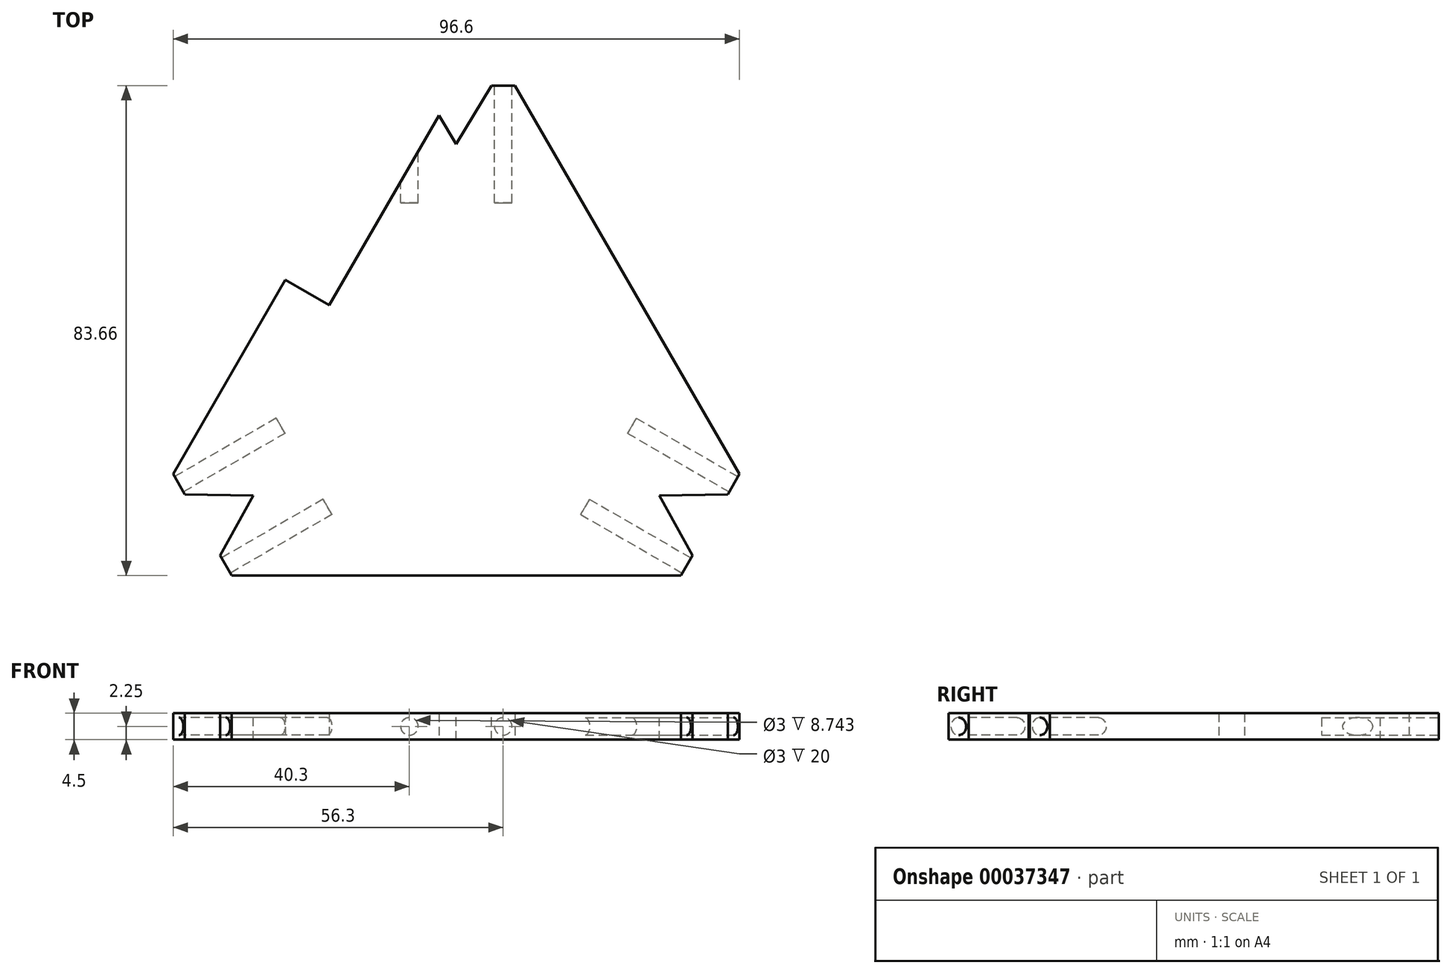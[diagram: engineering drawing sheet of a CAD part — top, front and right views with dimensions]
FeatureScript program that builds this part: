
annotation { "Feature Type Name" : "Feature", "Feature Type Description" : "" }
export const myFeature = defineFeature(function(context is Context, id is Id, definition is map)
    precondition{}
    {
        {
            var Q0;
            Q0=qCreatedBy(makeId("Top.planeOp"),FACE);
            var sketch = newSketch(context, id + "F0", { "sketchPlane" : qUnion([Q0])});
            skLineSegment(sketch, "E0.0", {"start": v(0, 50) * mm, "end": v(43.3, -25) * mm});
            skLineSegment(sketch, "E0.1", {"start": v(43.3, -25) * mm, "end": v(-43.3, -25) * mm});
            skCircle(sketch, "E1.cCircle", {"center": v(0, 0) * mm, "radius": 50 * mm, "construction": true});
            skLineSegment(sketch, "E1.0", {"start": v(-10, 50) * mm, "end": v(10, 50) * mm});
            skLineSegment(sketch, "E1.2", {"start": v(48.3, -16.34) * mm, "end": v(38.3, -33.66) * mm});
            skLineSegment(sketch, "E1.4", {"start": v(-38.3, -33.66) * mm, "end": v(-48.3, -16.34) * mm});
            skLineSegment(sketch, "E2", {"start": v(-10, 50) * mm, "end": v(-48.3, -16.34) * mm});
            skLineSegment(sketch, "E3", {"start": v(0, 50) * mm, "end": v(0, 0) * mm});
            skLineSegment(sketch, "E4.0.MirrorCS", {"start": v(10, 50) * mm, "end": v(48.3, -16.34) * mm});
            skLineSegment(sketch, "E5", {"start": v(-38.3, -33.66) * mm, "end": v(38.3, -33.66) * mm});
            skLineSegment(sketch, "E6", {"start": v(29.15, 16.83) * mm, "end": v(-43.3, -25) * mm});
            skLineSegment(sketch, "E7", {"start": v(43.3, -25) * mm, "end": v(-29.15, 16.83) * mm});
            skLineSegment(sketch, "E8.4.MirrorCS", {"start": v(0, 50) * mm, "end": v(-43.3, -25) * mm});
            skLineSegment(sketch, "E8.7.MirrorCS", {"start": v(-48.3, -16.34) * mm, "end": v(-38.3, -33.66) * mm});
            skLineSegment(sketch, "E9.11.MirrorCS", {"start": v(38.3, -33.66) * mm, "end": v(48.3, -16.34) * mm});
            skSolve(sketch);
        }
        {
            var Q0;
            {var subQ1=sQuery(id+"F0.wireOp",EDGE,"E0.1");var subQ4=sQuery(id+"F0.wireOp",EDGE,"c58d0613-940e-401f-9838-6fef4ca887ab.4.MirrorC");var subQ6=makeQuery(id+"F0.imprint","INTERSECT",VERTEX,{"disambiguationData":[OD(0.0)],"derivedFrom":[subQ1,subQ4]});Q0=makeQuery(id+"F0.imprint","IMPRINT",FACE,{"disambiguationData":[TD([[makeQuery(id+"F0.imprint","IMPRINT",EDGE,{"disambiguationData":[TD([[subQ6,-1.0]])],"derivedFrom":subQ1}),-1.0]])]});}
            var Q1;
            {var subQ0=sQuery(id+"F0.wireOp",EDGE,"5a5daee2-0941-4df6-baae-b4538d248986.2.MirrorC");var subQ1=sQuery(id+"F0.wireOp",EDGE,"E0.1");var subQ3=makeQuery(id+"F0.imprint","INTERSECT",VERTEX,{"disambiguationData":[OD(0.0)],"derivedFrom":[subQ1,subQ0]});Q1=makeQuery(id+"F0.imprint","IMPRINT",FACE,{"disambiguationData":[TD([[makeQuery(id+"F0.imprint","IMPRINT",EDGE,{"disambiguationData":[TD([[subQ3,-1.0]])],"derivedFrom":subQ1}),-1.0]])]});}
            var Q2;
            {var subQ1=sQuery(id+"F0.wireOp",EDGE,"E5");Q2=makeQuery(id+"F0.imprint","IMPRINT",FACE,{"disambiguationData":[TD([[makeQuery(id+"F0.imprint","IMPRINT",EDGE,{"derivedFrom":subQ1}),1.0]])]});}
            var Q3;
            {var subQ0=sQuery(id+"F0.wireOp",EDGE,"a30108d1-a80c-4c74-a365-e6b9bf17da23.3.MirrorC");var subQ1=sQuery(id+"F0.wireOp",EDGE,"E0.0");var subQ3=makeQuery(id+"F0.imprint","INTERSECT",VERTEX,{"disambiguationData":[OD(0.0)],"derivedFrom":[subQ1,subQ0]});Q3=makeQuery(id+"F0.imprint","IMPRINT",FACE,{"disambiguationData":[TD([[makeQuery(id+"F0.imprint","IMPRINT",EDGE,{"disambiguationData":[TD([[subQ3,-1.0]])],"derivedFrom":subQ1}),-1.0]])]});}
            var Q4;
            {var subQ1=sQuery(id+"F0.wireOp",EDGE,"E0.0");var subQ4=sQuery(id+"F0.wireOp",EDGE,"c58d0613-940e-401f-9838-6fef4ca887ab.0.MirrorC");var subQ6=makeQuery(id+"F0.imprint","INTERSECT",VERTEX,{"disambiguationData":[OD(0.0)],"derivedFrom":[subQ1,subQ4]});Q4=makeQuery(id+"F0.imprint","IMPRINT",FACE,{"disambiguationData":[TD([[makeQuery(id+"F0.imprint","IMPRINT",EDGE,{"disambiguationData":[TD([[subQ6,-1.0]])],"derivedFrom":subQ1}),-1.0]])]});}
            var Q5;
            {var subQ3=sQuery(id+"F0.wireOp",EDGE,"E8.4.MirrorCS");var subQ5=sQuery(id+"F0.wireOp",EDGE,"fde047dc-bef9-42db-b8b8-0a719749b1c3");var subQ7=makeQuery(id+"F0.imprint","INTERSECT",VERTEX,{"disambiguationData":[OD(0.0)],"derivedFrom":[subQ3,subQ5]});Q5=makeQuery(id+"F0.imprint","IMPRINT",FACE,{"disambiguationData":[TD([[makeQuery(id+"F0.imprint","IMPRINT",EDGE,{"disambiguationData":[TD([[subQ7,-1.0]])],"derivedFrom":subQ3}),-1.0]])]});}
            var Q6;
            {var subQ0=sQuery(id+"F0.wireOp",EDGE,"5a5daee2-0941-4df6-baae-b4538d248986.13.MirrorC");var subQ1=sQuery(id+"F0.wireOp",EDGE,"E8.4.MirrorCS");var subQ2=makeQuery(id+"F0.imprint","INTERSECT",VERTEX,{"disambiguationData":[OD(0.0)],"derivedFrom":[subQ1,subQ0]});Q6=makeQuery(id+"F0.imprint","IMPRINT",FACE,{"disambiguationData":[TD([[makeQuery(id+"F0.imprint","IMPRINT",EDGE,{"disambiguationData":[TD([[subQ2,-1.0]])],"derivedFrom":subQ1}),-1.0]])]});}
            var Q7;
            {var subQ8=sQuery(id+"F0.wireOp",EDGE,"E2");var subQ11=sQuery(id+"F0.wireOp",EDGE,"E7");var subQ13=makeQuery(id+"F0.imprint","INTERSECT",VERTEX,{"derivedFrom":[subQ11,subQ8]});Q7=makeQuery(id+"F0.imprint","IMPRINT",FACE,{"disambiguationData":[TD([[makeQuery(id+"F0.imprint","IMPRINT",EDGE,{"disambiguationData":[TD([[subQ13,1.0]])],"derivedFrom":subQ11}),1.0]])]});}
            var Q8;
            {var subQ0=sQuery(id+"F0.wireOp",EDGE,"c58d0613-940e-401f-9838-6fef4ca887ab.7.MirrorC");var subQ1=sQuery(id+"F0.wireOp",EDGE,"E0.1");var subQ3=makeQuery(id+"F0.imprint","INTERSECT",VERTEX,{"disambiguationData":[OD(0.0)],"derivedFrom":[subQ1,subQ0]});Q8=makeQuery(id+"F0.imprint","IMPRINT",FACE,{"disambiguationData":[TD([[makeQuery(id+"F0.imprint","IMPRINT",EDGE,{"disambiguationData":[TD([[subQ3,-1.0]])],"derivedFrom":subQ1}),-1.0]])]});}
            var Q9;
            {var subQ0=sQuery(id+"F0.wireOp",EDGE,"5a5daee2-0941-4df6-baae-b4538d248986.10.MirrorC");var subQ1=sQuery(id+"F0.wireOp",EDGE,"E0.1");var subQ3=makeQuery(id+"F0.imprint","INTERSECT",VERTEX,{"disambiguationData":[OD(0.0)],"derivedFrom":[subQ1,subQ0]});Q9=makeQuery(id+"F0.imprint","IMPRINT",FACE,{"disambiguationData":[TD([[makeQuery(id+"F0.imprint","IMPRINT",EDGE,{"disambiguationData":[TD([[subQ3,-1.0]])],"derivedFrom":subQ1}),-1.0]])]});}
            var Q10;
            {var subQ1=sQuery(id+"F0.wireOp",EDGE,"E8.4.MirrorCS");var subQ4=sQuery(id+"F0.wireOp",EDGE,"fde047dc-bef9-42db-b8b8-0a719749b1c3");var subQ6=makeQuery(id+"F0.imprint","INTERSECT",VERTEX,{"disambiguationData":[OD(0.0)],"derivedFrom":[subQ1,subQ4]});Q10=makeQuery(id+"F0.imprint","IMPRINT",FACE,{"disambiguationData":[TD([[makeQuery(id+"F0.imprint","IMPRINT",EDGE,{"disambiguationData":[TD([[subQ6,-1.0]])],"derivedFrom":subQ1}),1.0]])]});}
            var Q11;
            {var subQ0=sQuery(id+"F0.wireOp",EDGE,"5a5daee2-0941-4df6-baae-b4538d248986.13.MirrorC");var subQ1=sQuery(id+"F0.wireOp",EDGE,"E8.4.MirrorCS");var subQ3=makeQuery(id+"F0.imprint","INTERSECT",VERTEX,{"disambiguationData":[OD(0.0)],"derivedFrom":[subQ1,subQ0]});Q11=makeQuery(id+"F0.imprint","IMPRINT",FACE,{"disambiguationData":[TD([[makeQuery(id+"F0.imprint","IMPRINT",EDGE,{"disambiguationData":[TD([[subQ3,-1.0]])],"derivedFrom":subQ1}),1.0]])]});}
            var Q12;
            {var subQ3=sQuery(id+"F0.wireOp",EDGE,"E0.1");var subQ5=sQuery(id+"F0.wireOp",EDGE,"c58d0613-940e-401f-9838-6fef4ca887ab.4.MirrorC");var subQ6=makeQuery(id+"F0.imprint","INTERSECT",VERTEX,{"disambiguationData":[OD(0.0)],"derivedFrom":[subQ3,subQ5]});Q12=makeQuery(id+"F0.imprint","IMPRINT",FACE,{"disambiguationData":[TD([[makeQuery(id+"F0.imprint","IMPRINT",EDGE,{"disambiguationData":[TD([[subQ6,-1.0]])],"derivedFrom":subQ3}),1.0]])]});}
            var Q13;
            {var subQ3=sQuery(id+"F0.wireOp",EDGE,"E0.1");var subQ5=sQuery(id+"F0.wireOp",EDGE,"5a5daee2-0941-4df6-baae-b4538d248986.2.MirrorC");var subQ6=makeQuery(id+"F0.imprint","INTERSECT",VERTEX,{"disambiguationData":[OD(0.0)],"derivedFrom":[subQ3,subQ5]});Q13=makeQuery(id+"F0.imprint","IMPRINT",FACE,{"disambiguationData":[TD([[makeQuery(id+"F0.imprint","IMPRINT",EDGE,{"disambiguationData":[TD([[subQ6,-1.0]])],"derivedFrom":subQ3}),1.0]])]});}
            var Q14;
            {var subQ9=sQuery(id+"F0.wireOp",EDGE,"E2");var subQ10=sQuery(id+"F0.wireOp",EDGE,"E7");var subQ11=makeQuery(id+"F0.imprint","INTERSECT",VERTEX,{"derivedFrom":[subQ10,subQ9]});Q14=makeQuery(id+"F0.imprint","IMPRINT",FACE,{"disambiguationData":[TD([[makeQuery(id+"F0.imprint","IMPRINT",EDGE,{"disambiguationData":[TD([[subQ11,1.0]])],"derivedFrom":subQ10}),-1.0]])]});}
            var Q15;
            {var subQ3=sQuery(id+"F0.wireOp",EDGE,"c58d0613-940e-401f-9838-6fef4ca887ab.0.MirrorC");var subQ5=sQuery(id+"F0.wireOp",EDGE,"E0.0");var subQ7=makeQuery(id+"F0.imprint","INTERSECT",VERTEX,{"disambiguationData":[OD(0.0)],"derivedFrom":[subQ5,subQ3]});Q15=makeQuery(id+"F0.imprint","IMPRINT",FACE,{"disambiguationData":[TD([[makeQuery(id+"F0.imprint","IMPRINT",EDGE,{"disambiguationData":[TD([[subQ7,-1.0]])],"derivedFrom":subQ5}),1.0]])]});}
            var Q16;
            {var subQ1=sQuery(id+"F0.wireOp",EDGE,"E0.0");var subQ5=sQuery(id+"F0.wireOp",EDGE,"E6");var subQ8=makeQuery(id+"F0.imprint","INTERSECT",VERTEX,{"derivedFrom":[subQ1,subQ5]});Q16=makeQuery(id+"F0.imprint","IMPRINT",FACE,{"disambiguationData":[TD([[makeQuery(id+"F0.imprint","IMPRINT",EDGE,{"disambiguationData":[TD([[subQ8,-1.0]])],"derivedFrom":subQ1}),-1.0]])]});}
            var Q17;
            {var subQ0=sQuery(id+"F0.wireOp",EDGE,"4e667fc4-2969-494f-b06b-1dd07faa2963");var subQ1=sQuery(id+"F0.wireOp",EDGE,"E8.4.MirrorCS");var subQ3=makeQuery(id+"F0.imprint","INTERSECT",VERTEX,{"disambiguationData":[OD(0.0)],"derivedFrom":[subQ1,subQ0]});Q17=makeQuery(id+"F0.imprint","IMPRINT",FACE,{"disambiguationData":[TD([[makeQuery(id+"F0.imprint","IMPRINT",EDGE,{"disambiguationData":[TD([[subQ3,-1.0]])],"derivedFrom":subQ1}),1.0]])]});}
            var Q18;
            {var subQ0=sQuery(id+"F0.wireOp",EDGE,"5a5daee2-0941-4df6-baae-b4538d248986.4.MirrorC");var subQ1=sQuery(id+"F0.wireOp",EDGE,"E8.4.MirrorCS");var subQ3=makeQuery(id+"F0.imprint","INTERSECT",VERTEX,{"disambiguationData":[OD(0.0)],"derivedFrom":[subQ1,subQ0]});Q18=makeQuery(id+"F0.imprint","IMPRINT",FACE,{"disambiguationData":[TD([[makeQuery(id+"F0.imprint","IMPRINT",EDGE,{"disambiguationData":[TD([[subQ3,-1.0]])],"derivedFrom":subQ1}),1.0]])]});}
            var Q19;
            {var subQ0=sQuery(id+"F0.wireOp",EDGE,"a30108d1-a80c-4c74-a365-e6b9bf17da23.1.MirrorC");var subQ1=sQuery(id+"F0.wireOp",EDGE,"E0.0");var subQ3=makeQuery(id+"F0.imprint","INTERSECT",VERTEX,{"disambiguationData":[OD(0.0)],"derivedFrom":[subQ1,subQ0]});Q19=makeQuery(id+"F0.imprint","IMPRINT",FACE,{"disambiguationData":[TD([[makeQuery(id+"F0.imprint","IMPRINT",EDGE,{"disambiguationData":[TD([[subQ3,-1.0]])],"derivedFrom":subQ1}),-1.0]])]});}
            var Q20;
            {var subQ0=sQuery(id+"F0.wireOp",EDGE,"c58d0613-940e-401f-9838-6fef4ca887ab.5.MirrorC");var subQ1=sQuery(id+"F0.wireOp",EDGE,"E0.0");var subQ3=makeQuery(id+"F0.imprint","INTERSECT",VERTEX,{"disambiguationData":[OD(0.0)],"derivedFrom":[subQ1,subQ0]});Q20=makeQuery(id+"F0.imprint","IMPRINT",FACE,{"disambiguationData":[TD([[makeQuery(id+"F0.imprint","IMPRINT",EDGE,{"disambiguationData":[TD([[subQ3,-1.0]])],"derivedFrom":subQ1}),-1.0]])]});}
            var Q21;
            {var subQ3=sQuery(id+"F0.wireOp",EDGE,"E0.0");var subQ10=sQuery(id+"F0.wireOp",EDGE,"E6");var subQ11=makeQuery(id+"F0.imprint","INTERSECT",VERTEX,{"derivedFrom":[subQ3,subQ10]});Q21=makeQuery(id+"F0.imprint","IMPRINT",FACE,{"disambiguationData":[TD([[makeQuery(id+"F0.imprint","IMPRINT",EDGE,{"disambiguationData":[TD([[subQ11,-1.0]])],"derivedFrom":subQ3}),1.0]])]});}
            var Q22;
            {var subQ1=sQuery(id+"F0.wireOp",EDGE,"E0.0");var subQ5=sQuery(id+"F0.wireOp",EDGE,"a30108d1-a80c-4c74-a365-e6b9bf17da23.1.MirrorC");var subQ7=makeQuery(id+"F0.imprint","INTERSECT",VERTEX,{"disambiguationData":[OD(1.0)],"derivedFrom":[subQ1,subQ5]});Q22=makeQuery(id+"F0.imprint","IMPRINT",FACE,{"disambiguationData":[TD([[makeQuery(id+"F0.imprint","IMPRINT",EDGE,{"disambiguationData":[TD([[subQ7,-1.0]])],"derivedFrom":subQ1}),1.0]])]});}
            var Q23;
            {var subQ0=sQuery(id+"F0.wireOp",EDGE,"c58d0613-940e-401f-9838-6fef4ca887ab.5.MirrorC");var subQ3=sQuery(id+"F0.wireOp",EDGE,"E0.0");var subQ4=makeQuery(id+"F0.imprint","INTERSECT",VERTEX,{"disambiguationData":[OD(1.0)],"derivedFrom":[subQ3,subQ0]});Q23=makeQuery(id+"F0.imprint","IMPRINT",FACE,{"disambiguationData":[TD([[makeQuery(id+"F0.imprint","IMPRINT",EDGE,{"disambiguationData":[TD([[subQ4,-1.0]])],"derivedFrom":subQ3}),1.0]])]});}
            var Q24;
            {var subQ6=sQuery(id+"F0.wireOp",EDGE,"E3");Q24=makeQuery(id+"F0.imprint","IMPRINT",FACE,{"disambiguationData":[TD([[makeQuery(id+"F0.imprint","IMPRINT",EDGE,{"derivedFrom":subQ6}),1.0]])]});}
            var Q25;
            {var subQ1=sQuery(id+"F0.wireOp",EDGE,"E8.4.MirrorCS");var subQ6=sQuery(id+"F0.wireOp",EDGE,"E7");var subQ7=makeQuery(id+"F0.imprint","INTERSECT",VERTEX,{"derivedFrom":[subQ6,subQ1]});Q25=makeQuery(id+"F0.imprint","IMPRINT",FACE,{"disambiguationData":[TD([[makeQuery(id+"F0.imprint","IMPRINT",EDGE,{"disambiguationData":[TD([[subQ7,-1.0]])],"derivedFrom":subQ1}),1.0]])]});}
            var Q26;
            {var subQ6=sQuery(id+"F0.wireOp",EDGE,"E3");Q26=makeQuery(id+"F0.imprint","IMPRINT",FACE,{"disambiguationData":[TD([[makeQuery(id+"F0.imprint","IMPRINT",EDGE,{"derivedFrom":subQ6}),-1.0]])]});}
            var Q27;
            {var subQ1=sQuery(id+"F0.wireOp",EDGE,"E0.1");var subQ4=sQuery(id+"F0.wireOp",EDGE,"c58d0613-940e-401f-9838-6fef4ca887ab.4.MirrorC");var subQ5=makeQuery(id+"F0.imprint","INTERSECT",VERTEX,{"disambiguationData":[OD(1.0)],"derivedFrom":[subQ1,subQ4]});Q27=makeQuery(id+"F0.imprint","IMPRINT",FACE,{"disambiguationData":[TD([[makeQuery(id+"F0.imprint","IMPRINT",EDGE,{"disambiguationData":[TD([[subQ5,-1.0]])],"derivedFrom":subQ1}),-1.0]])]});}
            var Q28;
            {var subQ1=sQuery(id+"F0.wireOp",EDGE,"4e667fc4-2969-494f-b06b-1dd07faa2963");var subQ5=sQuery(id+"F0.wireOp",EDGE,"E8.4.MirrorCS");var subQ6=makeQuery(id+"F0.imprint","INTERSECT",VERTEX,{"disambiguationData":[OD(1.0)],"derivedFrom":[subQ5,subQ1]});Q28=makeQuery(id+"F0.imprint","IMPRINT",FACE,{"disambiguationData":[TD([[makeQuery(id+"F0.imprint","IMPRINT",EDGE,{"disambiguationData":[TD([[subQ6,-1.0]])],"derivedFrom":subQ5}),-1.0]])]});}
            var Q29;
            {var subQ1=sQuery(id+"F0.wireOp",EDGE,"E8.4.MirrorCS");var subQ5=sQuery(id+"F0.wireOp",EDGE,"5a5daee2-0941-4df6-baae-b4538d248986.4.MirrorC");var subQ7=makeQuery(id+"F0.imprint","INTERSECT",VERTEX,{"disambiguationData":[OD(1.0)],"derivedFrom":[subQ1,subQ5]});Q29=makeQuery(id+"F0.imprint","IMPRINT",FACE,{"disambiguationData":[TD([[makeQuery(id+"F0.imprint","IMPRINT",EDGE,{"disambiguationData":[TD([[subQ7,-1.0]])],"derivedFrom":subQ1}),-1.0]])]});}
            var Q30;
            {var subQ0=sQuery(id+"F0.wireOp",EDGE,"a30108d1-a80c-4c74-a365-e6b9bf17da23.3.MirrorC");var subQ1=sQuery(id+"F0.wireOp",EDGE,"E0.0");var subQ2=makeQuery(id+"F0.imprint","INTERSECT",VERTEX,{"disambiguationData":[OD(1.0)],"derivedFrom":[subQ1,subQ0]});Q30=makeQuery(id+"F0.imprint","IMPRINT",FACE,{"disambiguationData":[TD([[makeQuery(id+"F0.imprint","IMPRINT",EDGE,{"disambiguationData":[TD([[subQ2,-1.0]])],"derivedFrom":subQ1}),1.0]])]});}
            var Q31;
            {var subQ0=sQuery(id+"F0.wireOp",EDGE,"4e667fc4-2969-494f-b06b-1dd07faa2963");var subQ3=sQuery(id+"F0.wireOp",EDGE,"47e9f5c4-30d6-4785-8cf6-f1a65d77a122");var subQ4=makeQuery(id+"F0.imprint","INTERSECT",VERTEX,{"derivedFrom":[subQ3,subQ0]});Q31=makeQuery(id+"F0.imprint","IMPRINT",FACE,{"disambiguationData":[TD([[makeQuery(id+"F0.imprint","IMPRINT",EDGE,{"disambiguationData":[TD([[subQ4,-1.0]])],"derivedFrom":subQ0}),1.0]])]});}
            var Q32;
            {var subQ0=sQuery(id+"F0.wireOp",EDGE,"4e667fc4-2969-494f-b06b-1dd07faa2963");var subQ3=sQuery(id+"F0.wireOp",EDGE,"5f5b58d6-951e-4b7f-9c77-8e41affbd4cb");var subQ4=makeQuery(id+"F0.imprint","INTERSECT",VERTEX,{"derivedFrom":[subQ3,subQ0]});Q32=makeQuery(id+"F0.imprint","IMPRINT",FACE,{"disambiguationData":[TD([[makeQuery(id+"F0.imprint","IMPRINT",EDGE,{"disambiguationData":[TD([[subQ4,-1.0]])],"derivedFrom":subQ0}),1.0]])]});}
            var Q33;
            {var subQ0=sQuery(id+"F0.wireOp",EDGE,"4e667fc4-2969-494f-b06b-1dd07faa2963");var subQ3=sQuery(id+"F0.wireOp",EDGE,"E8.4.MirrorCS");var subQ4=makeQuery(id+"F0.imprint","INTERSECT",VERTEX,{"disambiguationData":[OD(0.0)],"derivedFrom":[subQ3,subQ0]});Q33=makeQuery(id+"F0.imprint","IMPRINT",FACE,{"disambiguationData":[TD([[makeQuery(id+"F0.imprint","IMPRINT",EDGE,{"disambiguationData":[TD([[subQ4,-1.0]])],"derivedFrom":subQ3}),-1.0]])]});}
            var Q34;
            {var subQ3=sQuery(id+"F0.wireOp",EDGE,"47e9f5c4-30d6-4785-8cf6-f1a65d77a122");var subQ5=sQuery(id+"F0.wireOp",EDGE,"fde047dc-bef9-42db-b8b8-0a719749b1c3");var subQ7=makeQuery(id+"F0.imprint","INTERSECT",VERTEX,{"derivedFrom":[subQ5,subQ3]});Q34=makeQuery(id+"F0.imprint","IMPRINT",FACE,{"disambiguationData":[TD([[makeQuery(id+"F0.imprint","IMPRINT",EDGE,{"disambiguationData":[TD([[subQ7,-1.0]])],"derivedFrom":subQ5}),1.0]])]});}
            var Q35;
            {var subQ3=sQuery(id+"F0.wireOp",EDGE,"5f5b58d6-951e-4b7f-9c77-8e41affbd4cb");var subQ5=sQuery(id+"F0.wireOp",EDGE,"fde047dc-bef9-42db-b8b8-0a719749b1c3");var subQ6=makeQuery(id+"F0.imprint","INTERSECT",VERTEX,{"derivedFrom":[subQ5,subQ3]});Q35=makeQuery(id+"F0.imprint","IMPRINT",FACE,{"disambiguationData":[TD([[makeQuery(id+"F0.imprint","IMPRINT",EDGE,{"disambiguationData":[TD([[subQ6,-1.0]])],"derivedFrom":subQ5}),1.0]])]});}
            var Q36;
            {var subQ0=sQuery(id+"F0.wireOp",EDGE,"a30108d1-a80c-4c74-a365-e6b9bf17da23.1.MirrorC");var subQ3=sQuery(id+"F0.wireOp",EDGE,"E0.0");var subQ7=makeQuery(id+"F0.imprint","INTERSECT",VERTEX,{"disambiguationData":[OD(0.0)],"derivedFrom":[subQ3,subQ0]});Q36=makeQuery(id+"F0.imprint","IMPRINT",FACE,{"disambiguationData":[TD([[makeQuery(id+"F0.imprint","IMPRINT",EDGE,{"disambiguationData":[TD([[subQ7,-1.0]])],"derivedFrom":subQ3}),1.0]])]});}
            var Q37;
            {var subQ1=sQuery(id+"F0.wireOp",EDGE,"a30108d1-a80c-4c74-a365-e6b9bf17da23.1.MirrorC");var subQ3=sQuery(id+"F0.wireOp",EDGE,"a30108d1-a80c-4c74-a365-e6b9bf17da23.0.MirrorCS");var subQ5=makeQuery(id+"F0.imprint","INTERSECT",VERTEX,{"derivedFrom":[subQ3,subQ1]});Q37=makeQuery(id+"F0.imprint","IMPRINT",FACE,{"disambiguationData":[TD([[makeQuery(id+"F0.imprint","IMPRINT",EDGE,{"disambiguationData":[TD([[subQ5,1.0]])],"derivedFrom":subQ1}),-1.0]])]});}
            var Q38;
            {var subQ0=sQuery(id+"F0.wireOp",EDGE,"a30108d1-a80c-4c74-a365-e6b9bf17da23.3.MirrorC");var subQ1=sQuery(id+"F0.wireOp",EDGE,"E0.0");var subQ2=makeQuery(id+"F0.imprint","INTERSECT",VERTEX,{"disambiguationData":[OD(0.0)],"derivedFrom":[subQ1,subQ0]});Q38=makeQuery(id+"F0.imprint","IMPRINT",FACE,{"disambiguationData":[TD([[makeQuery(id+"F0.imprint","IMPRINT",EDGE,{"disambiguationData":[TD([[subQ2,-1.0]])],"derivedFrom":subQ1}),1.0]])]});}
            var Q39;
            {var subQ0=sQuery(id+"F0.wireOp",EDGE,"a30108d1-a80c-4c74-a365-e6b9bf17da23.2.MirrorCS");var subQ1=sQuery(id+"F0.wireOp",EDGE,"a30108d1-a80c-4c74-a365-e6b9bf17da23.1.MirrorC");var subQ2=makeQuery(id+"F0.imprint","INTERSECT",VERTEX,{"derivedFrom":[subQ1,subQ0]});Q39=makeQuery(id+"F0.imprint","IMPRINT",FACE,{"disambiguationData":[TD([[makeQuery(id+"F0.imprint","IMPRINT",EDGE,{"disambiguationData":[TD([[subQ2,-1.0]])],"derivedFrom":subQ1}),-1.0]])]});}
            var Q40;
            {var subQ1=sQuery(id+"F0.wireOp",EDGE,"c58d0613-940e-401f-9838-6fef4ca887ab.7.MirrorC");var subQ5=sQuery(id+"F0.wireOp",EDGE,"E0.1");var subQ8=makeQuery(id+"F0.imprint","INTERSECT",VERTEX,{"disambiguationData":[OD(0.0)],"derivedFrom":[subQ5,subQ1]});Q40=makeQuery(id+"F0.imprint","IMPRINT",FACE,{"disambiguationData":[TD([[makeQuery(id+"F0.imprint","IMPRINT",EDGE,{"disambiguationData":[TD([[subQ8,-1.0]])],"derivedFrom":subQ5}),1.0]])]});}
            var Q41;
            {var subQ1=sQuery(id+"F0.wireOp",EDGE,"5a5daee2-0941-4df6-baae-b4538d248986.4.MirrorC");var subQ6=sQuery(id+"F0.wireOp",EDGE,"E8.4.MirrorCS");var subQ7=makeQuery(id+"F0.imprint","INTERSECT",VERTEX,{"disambiguationData":[OD(0.0)],"derivedFrom":[subQ6,subQ1]});Q41=makeQuery(id+"F0.imprint","IMPRINT",FACE,{"disambiguationData":[TD([[makeQuery(id+"F0.imprint","IMPRINT",EDGE,{"disambiguationData":[TD([[subQ7,-1.0]])],"derivedFrom":subQ6}),-1.0]])]});}
            var Q42;
            {var subQ0=sQuery(id+"F0.wireOp",EDGE,"5a5daee2-0941-4df6-baae-b4538d248986.10.MirrorC");var subQ3=sQuery(id+"F0.wireOp",EDGE,"5a5daee2-0941-4df6-baae-b4538d248986.5.MirrorCS");var subQ4=makeQuery(id+"F0.imprint","INTERSECT",VERTEX,{"derivedFrom":[subQ3,subQ0]});Q42=makeQuery(id+"F0.imprint","IMPRINT",FACE,{"disambiguationData":[TD([[makeQuery(id+"F0.imprint","IMPRINT",EDGE,{"disambiguationData":[TD([[subQ4,1.0]])],"derivedFrom":subQ0}),1.0]])]});}
            var Q43;
            {var subQ0=sQuery(id+"F0.wireOp",EDGE,"c58d0613-940e-401f-9838-6fef4ca887ab.8.MirrorCS");var subQ1=sQuery(id+"F0.wireOp",EDGE,"c58d0613-940e-401f-9838-6fef4ca887ab.5.MirrorC");var subQ2=makeQuery(id+"F0.imprint","INTERSECT",VERTEX,{"derivedFrom":[subQ1,subQ0]});Q43=makeQuery(id+"F0.imprint","IMPRINT",FACE,{"disambiguationData":[TD([[makeQuery(id+"F0.imprint","IMPRINT",EDGE,{"disambiguationData":[TD([[subQ2,-1.0]])],"derivedFrom":subQ1}),1.0]])]});}
            var Q44;
            {var subQ1=sQuery(id+"F0.wireOp",EDGE,"5a5daee2-0941-4df6-baae-b4538d248986.10.MirrorC");var subQ5=sQuery(id+"F0.wireOp",EDGE,"E0.1");var subQ8=makeQuery(id+"F0.imprint","INTERSECT",VERTEX,{"disambiguationData":[OD(0.0)],"derivedFrom":[subQ5,subQ1]});Q44=makeQuery(id+"F0.imprint","IMPRINT",FACE,{"disambiguationData":[TD([[makeQuery(id+"F0.imprint","IMPRINT",EDGE,{"disambiguationData":[TD([[subQ8,-1.0]])],"derivedFrom":subQ5}),1.0]])]});}
            var Q45;
            {var subQ1=sQuery(id+"F0.wireOp",EDGE,"c58d0613-940e-401f-9838-6fef4ca887ab.5.MirrorC");var subQ3=sQuery(id+"F0.wireOp",EDGE,"c58d0613-940e-401f-9838-6fef4ca887ab.2.MirrorCS");var subQ5=makeQuery(id+"F0.imprint","INTERSECT",VERTEX,{"derivedFrom":[subQ3,subQ1]});Q45=makeQuery(id+"F0.imprint","IMPRINT",FACE,{"disambiguationData":[TD([[makeQuery(id+"F0.imprint","IMPRINT",EDGE,{"disambiguationData":[TD([[subQ5,-1.0]])],"derivedFrom":subQ1}),1.0]])]});}
            var Q46;
            {var subQ1=sQuery(id+"F0.wireOp",EDGE,"5a5daee2-0941-4df6-baae-b4538d248986.4.MirrorC");var subQ3=sQuery(id+"F0.wireOp",EDGE,"5a5daee2-0941-4df6-baae-b4538d248986.7.MirrorCS");var subQ5=makeQuery(id+"F0.imprint","INTERSECT",VERTEX,{"derivedFrom":[subQ1,subQ3]});Q46=makeQuery(id+"F0.imprint","IMPRINT",FACE,{"disambiguationData":[TD([[makeQuery(id+"F0.imprint","IMPRINT",EDGE,{"disambiguationData":[TD([[subQ5,-1.0]])],"derivedFrom":subQ1}),-1.0]])]});}
            var Q47;
            {var subQ1=sQuery(id+"F0.wireOp",EDGE,"c58d0613-940e-401f-9838-6fef4ca887ab.5.MirrorC");var subQ5=sQuery(id+"F0.wireOp",EDGE,"E0.0");var subQ6=makeQuery(id+"F0.imprint","INTERSECT",VERTEX,{"disambiguationData":[OD(0.0)],"derivedFrom":[subQ5,subQ1]});Q47=makeQuery(id+"F0.imprint","IMPRINT",FACE,{"disambiguationData":[TD([[makeQuery(id+"F0.imprint","IMPRINT",EDGE,{"disambiguationData":[TD([[subQ6,-1.0]])],"derivedFrom":subQ5}),1.0]])]});}
            var Q48;
            {var subQ0=sQuery(id+"F0.wireOp",EDGE,"5a5daee2-0941-4df6-baae-b4538d248986.12.MirrorCS");var subQ1=sQuery(id+"F0.wireOp",EDGE,"5a5daee2-0941-4df6-baae-b4538d248986.4.MirrorC");var subQ2=makeQuery(id+"F0.imprint","INTERSECT",VERTEX,{"derivedFrom":[subQ1,subQ0]});Q48=makeQuery(id+"F0.imprint","IMPRINT",FACE,{"disambiguationData":[TD([[makeQuery(id+"F0.imprint","IMPRINT",EDGE,{"disambiguationData":[TD([[subQ2,-1.0]])],"derivedFrom":subQ1}),-1.0]])]});}
            var Q49;
            {var subQ0=sQuery(id+"F0.wireOp",EDGE,"c58d0613-940e-401f-9838-6fef4ca887ab.12.MirrorCS");var subQ1=sQuery(id+"F0.wireOp",EDGE,"c58d0613-940e-401f-9838-6fef4ca887ab.7.MirrorC");var subQ2=makeQuery(id+"F0.imprint","INTERSECT",VERTEX,{"derivedFrom":[subQ1,subQ0]});Q49=makeQuery(id+"F0.imprint","IMPRINT",FACE,{"disambiguationData":[TD([[makeQuery(id+"F0.imprint","IMPRINT",EDGE,{"disambiguationData":[TD([[subQ2,-1.0]])],"derivedFrom":subQ1}),-1.0]])]});}
            var Q50;
            {var subQ1=sQuery(id+"F0.wireOp",EDGE,"c58d0613-940e-401f-9838-6fef4ca887ab.7.MirrorC");var subQ3=sQuery(id+"F0.wireOp",EDGE,"c58d0613-940e-401f-9838-6fef4ca887ab.3.MirrorCS");var subQ5=makeQuery(id+"F0.imprint","INTERSECT",VERTEX,{"derivedFrom":[subQ3,subQ1]});Q50=makeQuery(id+"F0.imprint","IMPRINT",FACE,{"disambiguationData":[TD([[makeQuery(id+"F0.imprint","IMPRINT",EDGE,{"disambiguationData":[TD([[subQ5,-1.0]])],"derivedFrom":subQ1}),-1.0]])]});}
            var Q51;
            {var subQ1=sQuery(id+"F0.wireOp",EDGE,"5a5daee2-0941-4df6-baae-b4538d248986.10.MirrorC");var subQ3=sQuery(id+"F0.wireOp",EDGE,"5a5daee2-0941-4df6-baae-b4538d248986.8.MirrorCS");var subQ5=makeQuery(id+"F0.imprint","INTERSECT",VERTEX,{"derivedFrom":[subQ3,subQ1]});Q51=makeQuery(id+"F0.imprint","IMPRINT",FACE,{"disambiguationData":[TD([[makeQuery(id+"F0.imprint","IMPRINT",EDGE,{"disambiguationData":[TD([[subQ5,1.0]])],"derivedFrom":subQ1}),1.0]])]});}
            var Q52;
            {var subQ3=sQuery(id+"F0.wireOp",EDGE,"5a5daee2-0941-4df6-baae-b4538d248986.2.MirrorC");var subQ5=sQuery(id+"F0.wireOp",EDGE,"5a5daee2-0941-4df6-baae-b4538d248986.8.MirrorCS");var subQ7=makeQuery(id+"F0.imprint","INTERSECT",VERTEX,{"derivedFrom":[subQ3,subQ5]});Q52=makeQuery(id+"F0.imprint","IMPRINT",FACE,{"disambiguationData":[TD([[makeQuery(id+"F0.imprint","IMPRINT",EDGE,{"disambiguationData":[TD([[subQ7,1.0]])],"derivedFrom":subQ3}),1.0]])]});}
            var Q53;
            {var subQ3=sQuery(id+"F0.wireOp",EDGE,"5a5daee2-0941-4df6-baae-b4538d248986.5.MirrorCS");var subQ5=sQuery(id+"F0.wireOp",EDGE,"5a5daee2-0941-4df6-baae-b4538d248986.2.MirrorC");var subQ7=makeQuery(id+"F0.imprint","INTERSECT",VERTEX,{"derivedFrom":[subQ5,subQ3]});Q53=makeQuery(id+"F0.imprint","IMPRINT",FACE,{"disambiguationData":[TD([[makeQuery(id+"F0.imprint","IMPRINT",EDGE,{"disambiguationData":[TD([[subQ7,1.0]])],"derivedFrom":subQ5}),1.0]])]});}
            var Q54;
            {var subQ0=sQuery(id+"F0.wireOp",EDGE,"a30108d1-a80c-4c74-a365-e6b9bf17da23.3.MirrorC");var subQ3=sQuery(id+"F0.wireOp",EDGE,"a30108d1-a80c-4c74-a365-e6b9bf17da23.0.MirrorCS");var subQ4=makeQuery(id+"F0.imprint","INTERSECT",VERTEX,{"derivedFrom":[subQ3,subQ0]});Q54=makeQuery(id+"F0.imprint","IMPRINT",FACE,{"disambiguationData":[TD([[makeQuery(id+"F0.imprint","IMPRINT",EDGE,{"disambiguationData":[TD([[subQ4,1.0]])],"derivedFrom":subQ3}),1.0]])]});}
            var Q55;
            {var subQ3=sQuery(id+"F0.wireOp",EDGE,"c58d0613-940e-401f-9838-6fef4ca887ab.4.MirrorC");var subQ5=sQuery(id+"F0.wireOp",EDGE,"c58d0613-940e-401f-9838-6fef4ca887ab.3.MirrorCS");var subQ7=makeQuery(id+"F0.imprint","INTERSECT",VERTEX,{"derivedFrom":[subQ5,subQ3]});Q55=makeQuery(id+"F0.imprint","IMPRINT",FACE,{"disambiguationData":[TD([[makeQuery(id+"F0.imprint","IMPRINT",EDGE,{"disambiguationData":[TD([[subQ7,1.0]])],"derivedFrom":subQ5}),-1.0]])]});}
            var Q56;
            {var subQ3=sQuery(id+"F0.wireOp",EDGE,"c58d0613-940e-401f-9838-6fef4ca887ab.4.MirrorC");var subQ5=sQuery(id+"F0.wireOp",EDGE,"c58d0613-940e-401f-9838-6fef4ca887ab.9.MirrorCS");var subQ7=makeQuery(id+"F0.imprint","INTERSECT",VERTEX,{"derivedFrom":[subQ3,subQ5]});Q56=makeQuery(id+"F0.imprint","IMPRINT",FACE,{"disambiguationData":[TD([[makeQuery(id+"F0.imprint","IMPRINT",EDGE,{"disambiguationData":[TD([[subQ7,1.0]])],"derivedFrom":subQ3}),-1.0]])]});}
            var Q57;
            {var subQ1=sQuery(id+"F0.wireOp",EDGE,"a30108d1-a80c-4c74-a365-e6b9bf17da23.1.MirrorC");var subQ5=sQuery(id+"F0.wireOp",EDGE,"a30108d1-a80c-4c74-a365-e6b9bf17da23.2.MirrorCS");var subQ7=makeQuery(id+"F0.imprint","INTERSECT",VERTEX,{"derivedFrom":[subQ1,subQ5]});Q57=makeQuery(id+"F0.imprint","IMPRINT",FACE,{"disambiguationData":[TD([[makeQuery(id+"F0.imprint","IMPRINT",EDGE,{"disambiguationData":[TD([[subQ7,-1.0]])],"derivedFrom":subQ1}),1.0]])]});}
            var Q58;
            {var subQ1=sQuery(id+"F0.wireOp",EDGE,"5a5daee2-0941-4df6-baae-b4538d248986.10.MirrorC");var subQ5=sQuery(id+"F0.wireOp",EDGE,"E0.1");var subQ6=makeQuery(id+"F0.imprint","INTERSECT",VERTEX,{"disambiguationData":[OD(1.0)],"derivedFrom":[subQ5,subQ1]});Q58=makeQuery(id+"F0.imprint","IMPRINT",FACE,{"disambiguationData":[TD([[makeQuery(id+"F0.imprint","IMPRINT",EDGE,{"disambiguationData":[TD([[subQ6,-1.0]])],"derivedFrom":subQ5}),1.0]])]});}
            var Q59;
            {var subQ3=sQuery(id+"F0.wireOp",EDGE,"c58d0613-940e-401f-9838-6fef4ca887ab.0.MirrorC");var subQ5=sQuery(id+"F0.wireOp",EDGE,"c58d0613-940e-401f-9838-6fef4ca887ab.2.MirrorCS");var subQ7=makeQuery(id+"F0.imprint","INTERSECT",VERTEX,{"derivedFrom":[subQ3,subQ5]});Q59=makeQuery(id+"F0.imprint","IMPRINT",FACE,{"disambiguationData":[TD([[makeQuery(id+"F0.imprint","IMPRINT",EDGE,{"disambiguationData":[TD([[subQ7,-1.0]])],"derivedFrom":subQ3}),1.0]])]});}
            var Q60;
            {var subQ1=sQuery(id+"F0.wireOp",EDGE,"5a5daee2-0941-4df6-baae-b4538d248986.4.MirrorC");var subQ5=sQuery(id+"F0.wireOp",EDGE,"5a5daee2-0941-4df6-baae-b4538d248986.7.MirrorCS");var subQ7=makeQuery(id+"F0.imprint","INTERSECT",VERTEX,{"derivedFrom":[subQ1,subQ5]});Q60=makeQuery(id+"F0.imprint","IMPRINT",FACE,{"disambiguationData":[TD([[makeQuery(id+"F0.imprint","IMPRINT",EDGE,{"disambiguationData":[TD([[subQ7,-1.0]])],"derivedFrom":subQ1}),1.0]])]});}
            var Q61;
            {var subQ1=sQuery(id+"F0.wireOp",EDGE,"5a5daee2-0941-4df6-baae-b4538d248986.12.MirrorCS");var subQ5=sQuery(id+"F0.wireOp",EDGE,"5a5daee2-0941-4df6-baae-b4538d248986.4.MirrorC");var subQ6=makeQuery(id+"F0.imprint","INTERSECT",VERTEX,{"derivedFrom":[subQ5,subQ1]});Q61=makeQuery(id+"F0.imprint","IMPRINT",FACE,{"disambiguationData":[TD([[makeQuery(id+"F0.imprint","IMPRINT",EDGE,{"disambiguationData":[TD([[subQ6,-1.0]])],"derivedFrom":subQ5}),1.0]])]});}
            var Q62;
            {var subQ3=sQuery(id+"F0.wireOp",EDGE,"c58d0613-940e-401f-9838-6fef4ca887ab.0.MirrorC");var subQ5=sQuery(id+"F0.wireOp",EDGE,"c58d0613-940e-401f-9838-6fef4ca887ab.6.MirrorCS");var subQ7=makeQuery(id+"F0.imprint","INTERSECT",VERTEX,{"derivedFrom":[subQ3,subQ5]});Q62=makeQuery(id+"F0.imprint","IMPRINT",FACE,{"disambiguationData":[TD([[makeQuery(id+"F0.imprint","IMPRINT",EDGE,{"disambiguationData":[TD([[subQ7,1.0]])],"derivedFrom":subQ3}),1.0]])]});}
            var Q63;
            {var subQ1=sQuery(id+"F0.wireOp",EDGE,"c58d0613-940e-401f-9838-6fef4ca887ab.7.MirrorC");var subQ5=sQuery(id+"F0.wireOp",EDGE,"E0.1");var subQ6=makeQuery(id+"F0.imprint","INTERSECT",VERTEX,{"disambiguationData":[OD(1.0)],"derivedFrom":[subQ5,subQ1]});Q63=makeQuery(id+"F0.imprint","IMPRINT",FACE,{"disambiguationData":[TD([[makeQuery(id+"F0.imprint","IMPRINT",EDGE,{"disambiguationData":[TD([[subQ6,-1.0]])],"derivedFrom":subQ5}),1.0]])]});}
            var Q64;
            {var subQ3=sQuery(id+"F0.wireOp",EDGE,"E4.0.MirrorCS");var subQ5=sQuery(id+"F0.wireOp",EDGE,"E1.0");var subQ6=makeQuery(id+"F0.imprint","INTERSECT",VERTEX,{"derivedFrom":[subQ5,subQ3]});Q64=makeQuery(id+"F0.imprint","IMPRINT",FACE,{"disambiguationData":[TD([[makeQuery(id+"F0.imprint","IMPRINT",EDGE,{"disambiguationData":[TD([[subQ6,-1.0]])],"derivedFrom":subQ3}),-1.0]])]});}
            extrude(context, id + "F1", {"entities" : qUnion([Q0, Q1, Q2, Q3, Q4, Q5, Q6, Q7, Q8, Q9, Q10, Q11, Q12, Q13, Q14, Q15, Q16, Q17, Q18, Q19, Q20, Q21, Q22, Q23, Q24, Q25, Q26, Q27, Q28, Q29, Q30, Q31, Q32, Q33, Q34, Q35, Q36, Q37, Q38, Q39, Q40, Q41, Q42, Q43, Q44, Q45, Q46, Q47, Q48, Q49, Q50, Q51, Q52, Q53, Q54, Q55, Q56, Q57, Q58, Q59, Q60, Q61, Q62, Q63, Q64]), "depth" : 2.25 * mm, "hasSecondDirection" : true, "secondDirectionOppositeDirection" : true, "secondDirectionDepth" : 2.25 * mm});
        }
        {
            var Q0;
            Q0=makeQuery(id+"F1.opExtrude","SWEPT_FACE",FACE,{"disambiguationData":[OSD([sQuery(id+"F0.wireOp",EDGE,"E1.0")])]});
            var sketch = newSketch(context, id + "F2", { "sketchPlane" : qUnion([Q0])});
            skCircle(sketch, "E10", {"center": v(-8, 0) * mm, "radius": 1.5 * mm});
            skPoint(sketch, "E11", {"position": v(0, 0) * mm});
            skPoint(sketch, "E12", {"position": v(-8, 1.5) * mm});
            skLineSegment(sketch, "E13", {"start": v(-8, 0) * mm, "end": v(-8, 1.5) * mm});
            skLineSegment(sketch, "E14", {"start": v(-8, 0) * mm, "end": v(0, 0) * mm});
            skLineSegment(sketch, "E15", {"start": v(-8, 0) * mm, "end": v(-10, 0) * mm});
            skPoint(sketch, "E16.0.MirrorP", {"position": v(8, 1.5) * mm});
            skCircle(sketch, "E16.2.MirrorC", {"center": v(8, 0) * mm, "radius": 1.5 * mm});
            skLineSegment(sketch, "E16.3.MirrorCS", {"start": v(8, 0) * mm, "end": v(8, 1.5) * mm});
            skLineSegment(sketch, "E16.4.MirrorCS", {"start": v(8, 0) * mm, "end": v(10, 0) * mm});
            skLineSegment(sketch, "E16.5.MirrorCS", {"start": v(8, 0) * mm, "end": v(0, 0) * mm});
            skSolve(sketch);
        }
        {
            var Q0;
            Q0=qSketchRegion(id+"F2",true);
            extrude(context, id + "F3", {"entities" : qUnion([Q0]), "oppositeDirection" : true, "depth" : 20 * mm});
        }
        {
            var Q0;
            Q0=sQuery(id+"F0.wireOp",EDGE,"E7");
            cPlane(context, id + "F4", {"entities" : qUnion([Q0]), "cplaneType" : CPlaneType.LINE_ANGLE, "offset" : 150 * mm, "angle" : 0 * degree, "width" : 150 * mm, "height" : 150 * mm});
        }
        {
            var Q0;
            Q0=sQuery(id+"F0.wireOp",EDGE,"E6");
            cPlane(context, id + "F5", {"entities" : qUnion([Q0]), "cplaneType" : CPlaneType.LINE_ANGLE, "offset" : 150 * mm, "angle" : 0 * degree, "width" : 150 * mm, "height" : 150 * mm});
        }
        {
            var Q0;
            Q0=makeQuery(id+"F3.opExtrude","SWEPT_BODY",BODY,{"disambiguationData":[OSD([sQuery(id+"F2.wireOp",EDGE,"E10")])]});
            var Q1;
            Q1=makeQuery(id+"F3.opExtrude","SWEPT_BODY",BODY,{"disambiguationData":[OSD([sQuery(id+"F2.wireOp",EDGE,"E16.2.MirrorC")])]});
            var Q2;
            Q2=qCreatedBy(id+"F5.planeOp",FACE);
            mirror(context, id + "F6", {"entities" : qUnion([Q0, Q1]), "mirrorPlane" : qUnion([Q2])});
        }
        {
            var Q0;
            Q0=makeQuery(id+"F3.opExtrude","SWEPT_BODY",BODY,{"disambiguationData":[OSD([sQuery(id+"F2.wireOp",EDGE,"E10")])]});
            var Q1;
            Q1=makeQuery(id+"F3.opExtrude","SWEPT_BODY",BODY,{"disambiguationData":[OSD([sQuery(id+"F2.wireOp",EDGE,"E16.2.MirrorC")])]});
            var Q2;
            Q2=qCreatedBy(id+"F4.planeOp",FACE);
            mirror(context, id + "F7", {"entities" : qUnion([Q0, Q1]), "mirrorPlane" : qUnion([Q2])});
        }
        {
            var Q0;
            Q0=makeQuery(id+"F3.opExtrude","SWEPT_BODY",BODY,{"disambiguationData":[OSD([sQuery(id+"F2.wireOp",EDGE,"E10")])]});
            var Q1;
            Q1=makeQuery(id+"F3.opExtrude","SWEPT_BODY",BODY,{"disambiguationData":[OSD([sQuery(id+"F2.wireOp",EDGE,"E16.2.MirrorC")])]});
            var Q2;
            Q2=makeQuery(id+"F6.opPattern","COPY",BODY,{"derivedFrom":makeQuery(id+"F3.opExtrude","SWEPT_BODY",BODY,{"disambiguationData":[OSD([sQuery(id+"F2.wireOp",EDGE,"E10")])]}),"instanceName":"1"});
            var Q3;
            Q3=makeQuery(id+"F6.opPattern","COPY",BODY,{"derivedFrom":makeQuery(id+"F3.opExtrude","SWEPT_BODY",BODY,{"disambiguationData":[OSD([sQuery(id+"F2.wireOp",EDGE,"E16.2.MirrorC")])]}),"instanceName":"1"});
            var Q4;
            Q4=makeQuery(id+"F7.opPattern","COPY",BODY,{"derivedFrom":makeQuery(id+"F3.opExtrude","SWEPT_BODY",BODY,{"disambiguationData":[OSD([sQuery(id+"F2.wireOp",EDGE,"E16.2.MirrorC")])]}),"instanceName":"1"});
            var Q5;
            Q5=makeQuery(id+"F7.opPattern","COPY",BODY,{"derivedFrom":makeQuery(id+"F3.opExtrude","SWEPT_BODY",BODY,{"disambiguationData":[OSD([sQuery(id+"F2.wireOp",EDGE,"E10")])]}),"instanceName":"1"});
            var Q6;
            Q6=makeQuery(id+"F1.opExtrude","SWEPT_BODY",BODY,{"disambiguationData":[OSD([sQuery(id+"F0.wireOp",EDGE,"E1.0"),sQuery(id+"F0.wireOp",EDGE,"E4.0.MirrorCS"),sQuery(id+"F0.wireOp",EDGE,"E5"),sQuery(id+"F0.wireOp",EDGE,"E2"),sQuery(id+"F0.wireOp",EDGE,"E9.11.MirrorCS"),sQuery(id+"F0.wireOp",EDGE,"E8.7.MirrorCS")])]});
            booleanBodies(context, id + "F8", {"operationType" : BooleanOperationType.SUBTRACTION, "tools" : qUnion([Q0, Q1, Q2, Q3, Q4, Q5]), "targets" : qUnion([Q6])});
        }
        {
            var Q0;
            Q0=qCreatedBy(makeId("Top.planeOp"),FACE);
            var sketch = newSketch(context, id + "F9", { "sketchPlane" : qUnion([Q0])});
            skLineSegment(sketch, "E17", {"start": v(-6, 50) * mm, "end": v(0, 40) * mm});
            skLineSegment(sketch, "E18", {"start": v(0, 40) * mm, "end": v(6, 50) * mm});
            skLineSegment(sketch, "E19", {"start": v(0, 40) * mm, "end": v(0, 50) * mm});
            skLineSegment(sketch, "E20", {"start": v(-6, 50) * mm, "end": v(0, 50) * mm});
            skLineSegment(sketch, "E21", {"start": v(0, 50) * mm, "end": v(6, 50) * mm});
            skLineSegment(sketch, "E22.0.MirrorCS", {"start": v(-34.64, -20) * mm, "end": v(-40.3, -30.2) * mm});
            skLineSegment(sketch, "E22.1.MirrorCS", {"start": v(-43.3, -25) * mm, "end": v(-40.3, -30.2) * mm});
            skLineSegment(sketch, "E22.2.MirrorCS", {"start": v(-34.64, -20) * mm, "end": v(-43.3, -25) * mm});
            skLineSegment(sketch, "E22.3.MirrorCS", {"start": v(-46.3, -19.8) * mm, "end": v(-43.3, -25) * mm});
            skLineSegment(sketch, "E22.4.MirrorCS", {"start": v(-46.3, -19.8) * mm, "end": v(-34.64, -20) * mm});
            skLineSegment(sketch, "E23.0.MirrorCS", {"start": v(43.3, -25) * mm, "end": v(46.3, -19.8) * mm});
            skLineSegment(sketch, "E23.1.MirrorCS", {"start": v(40.3, -30.2) * mm, "end": v(43.3, -25) * mm});
            skLineSegment(sketch, "E23.2.MirrorCS", {"start": v(40.3, -30.2) * mm, "end": v(34.64, -20) * mm});
            skLineSegment(sketch, "E23.3.MirrorCS", {"start": v(34.64, -20) * mm, "end": v(46.3, -19.8) * mm});
            skLineSegment(sketch, "E23.4.MirrorCS", {"start": v(34.64, -20) * mm, "end": v(43.3, -25) * mm});
            skSolve(sketch);
        }
        {
            var Q0;
            Q0=qSketchRegion(id+"F9",true);
            extrude(context, id + "F10", {"entities" : qUnion([Q0]), "operationType" : NewBodyOperationType.REMOVE, "endBound" : BoundingType.THROUGH_ALL, "oppositeDirection" : true, "depth" : 25 * mm, "hasSecondDirection" : true, "secondDirectionOppositeDirection" : false, "secondDirectionDepth" : 25 * mm});
        }
    });
